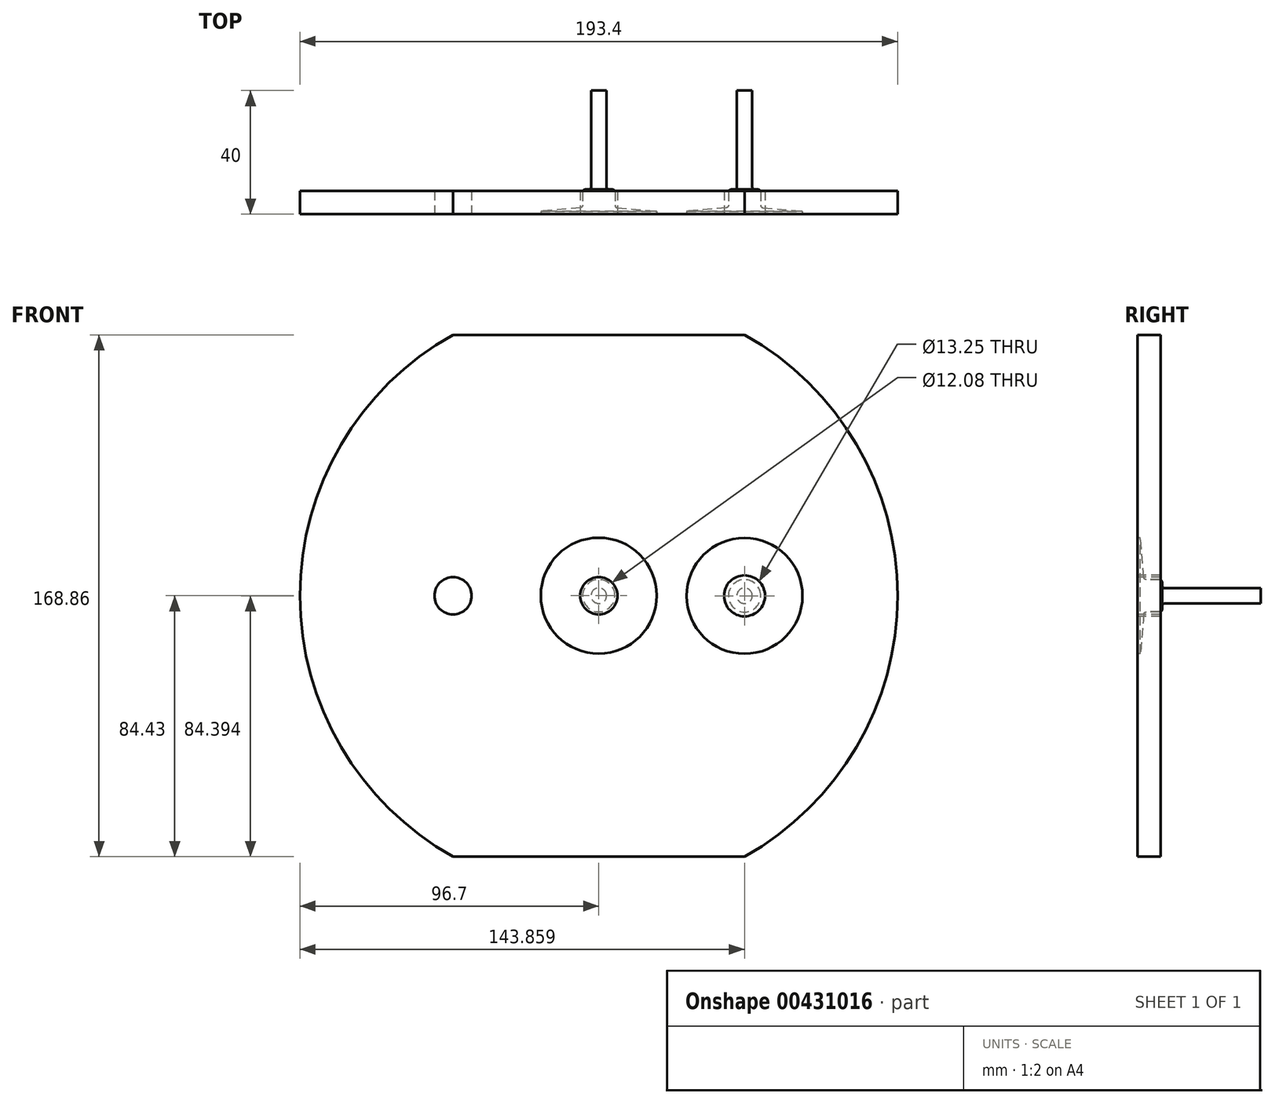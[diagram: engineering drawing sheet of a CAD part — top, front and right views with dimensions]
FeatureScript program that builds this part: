
annotation { "Feature Type Name" : "Feature", "Feature Type Description" : "" }
export const myFeature = defineFeature(function(context is Context, id is Id, definition is map)
    precondition{}
    {
        {
            var Q0;
            Q0=qCreatedBy(makeId("Front.planeOp"),FACE);
            var sketch = newSketch(context, id + "F0", { "sketchPlane" : qUnion([Q0])});
            skCircle(sketch, "E0", {"center": v(0, 0) * mm, "radius": 5.22 * mm});
            skPoint(sketch, "E0.first.point", {"position": v(-0.14, 5.22) * mm});
            skPoint(sketch, "E0.second.point", {"position": v(0.18, -5.22) * mm});
            skPoint(sketch, "E0.third.point", {"position": v(5.22, 0.15) * mm});
            skSolve(sketch);
        }
        {
            var Q0;
            Q0=qCreatedBy(makeId("Front.planeOp"),FACE);
            var sketch = newSketch(context, id + "F1", { "sketchPlane" : qUnion([Q0])});
            skCircle(sketch, "E1.0", {"center": v(0, 0) * mm, "radius": 5.22 * mm});
            skLineSegment(sketch, "E2", {"start": v(0, 125) * mm, "end": v(0, -125) * mm, "construction": true});
            skLineSegment(sketch, "E3", {"start": v(-125, 0) * mm, "end": v(125, 0) * mm, "construction": true});
            skArc(sketch, "E4", {"start": v(-3.61, 24.74) * mm, "mid": v(1.57, -24.95) * mm, "end": v(0.48, 25) * mm, "construction": true});
            skCircle(sketch, "E5", {"center": v(0, 0) * mm, "radius": 23.24 * mm, "construction": true});
            skCircle(sketch, "E6", {"center": v(0, 0) * mm, "radius": 21.43 * mm, "construction": true});
            skLineSegment(sketch, "E7", {"start": v(0, 0) * mm, "end": v(-4.4, 25.96) * mm, "construction": true});
            skLineSegment(sketch, "E8", {"start": v(0, 0) * mm, "end": v(1.13, 26.88) * mm, "construction": true});
            skFitSpline(sketch, "E9", {"points": [v(-3.61, 24.74) * mm, v(-2.7, 23.08) * mm, v(-2.2, 21.32) * mm, v(-1.5, 20.62) * mm], "startDerivative": vector(3.33, -4.08) * mm, "endDerivative": vector(3.08, -2.02) * mm});
            skFitSpline(sketch, "E10.MirrorCS", {"points": [v(0.48, 25) * mm, v(-0.2, 23.23) * mm, v(-0.5, 21.43) * mm, v(-1.1, 20.65) * mm], "startDerivative": vector(-2.8, -4.47) * mm, "endDerivative": vector(-2.8, -2.4) * mm});
            skArc(sketch, "E11", {"start": v(-2.2, 21.32) * mm, "mid": v(-1.35, 21.39) * mm, "end": v(-0.5, 21.43) * mm});
            skArc(sketch, "E12", {"start": v(-4.17, 24.65) * mm, "mid": v(-3.9, 24.7) * mm, "end": v(-3.61, 24.74) * mm});
            skArc(sketch, "E13.trimOffspring", {"start": v(0.48, 25) * mm, "mid": v(0.77, 24.99) * mm, "end": v(1.05, 24.98) * mm});
            skArc(sketch, "E14.1.0", {"start": v(-4.72, 24.55) * mm, "mid": v(-4.45, 24.6) * mm, "end": v(-4.17, 24.65) * mm});
            skArc(sketch, "E14.1.1", {"start": v(-9.2, 23.24) * mm, "mid": v(-8.94, 23.35) * mm, "end": v(-8.68, 23.45) * mm});
            skArc(sketch, "E14.1.2", {"start": v(-6.58, 20.4) * mm, "mid": v(-5.76, 20.64) * mm, "end": v(-4.94, 20.86) * mm});
            skArc(sketch, "E14.2.0", {"start": v(-9.72, 23.03) * mm, "mid": v(-9.46, 23.14) * mm, "end": v(-9.2, 23.24) * mm});
            skArc(sketch, "E14.2.1", {"start": v(-13.84, 20.82) * mm, "mid": v(-13.6, 20.98) * mm, "end": v(-13.36, 21.13) * mm});
            skArc(sketch, "E14.2.2", {"start": v(-10.68, 18.58) * mm, "mid": v(-9.93, 19) * mm, "end": v(-9.16, 19.37) * mm});
            skArc(sketch, "E14.3.0", {"start": v(-14.3, 20.5) * mm, "mid": v(-14.07, 20.67) * mm, "end": v(-13.84, 20.82) * mm});
            skArc(sketch, "E14.3.1", {"start": v(-17.86, 17.5) * mm, "mid": v(-17.66, 17.7) * mm, "end": v(-17.46, 17.89) * mm});
            skArc(sketch, "E14.3.2", {"start": v(-14.3, 15.96) * mm, "mid": v(-13.66, 16.51) * mm, "end": v(-13, 17.04) * mm});
            skArc(sketch, "E14.4.0", {"start": v(-18.25, 17.08) * mm, "mid": v(-18.06, 17.29) * mm, "end": v(-17.86, 17.5) * mm});
            skArc(sketch, "E14.4.1", {"start": v(-21.1, 13.4) * mm, "mid": v(-20.96, 13.63) * mm, "end": v(-20.8, 13.87) * mm});
            skArc(sketch, "E14.4.2", {"start": v(-17.31, 12.63) * mm, "mid": v(-16.8, 13.31) * mm, "end": v(-16.25, 13.97) * mm});
            skArc(sketch, "E14.5.0", {"start": v(-21.4, 12.92) * mm, "mid": v(-21.26, 13.16) * mm, "end": v(-21.1, 13.4) * mm});
            skArc(sketch, "E14.5.1", {"start": v(-23.43, 8.71) * mm, "mid": v(-23.33, 8.98) * mm, "end": v(-23.23, 9.24) * mm});
            skArc(sketch, "E14.5.2", {"start": v(-19.56, 8.76) * mm, "mid": v(-19.2, 9.53) * mm, "end": v(-18.8, 10.29) * mm});
            skArc(sketch, "E14.6.0", {"start": v(-23.62, 8.18) * mm, "mid": v(-23.53, 8.45) * mm, "end": v(-23.43, 8.71) * mm});
            skArc(sketch, "E14.6.1", {"start": v(-24.73, 3.65) * mm, "mid": v(-24.69, 3.93) * mm, "end": v(-24.64, 4.2) * mm});
            skArc(sketch, "E14.6.2", {"start": v(-20.95, 4.5) * mm, "mid": v(-20.76, 5.33) * mm, "end": v(-20.53, 6.15) * mm});
            skArc(sketch, "E14.7.0", {"start": v(-24.8, 3.1) * mm, "mid": v(-24.77, 3.37) * mm, "end": v(-24.73, 3.65) * mm});
            skArc(sketch, "E14.7.1", {"start": v(-24.95, -1.57) * mm, "mid": v(-24.97, -1.29) * mm, "end": v(-24.98, -1) * mm});
            skArc(sketch, "E14.7.2", {"start": v(-21.43, 0.04) * mm, "mid": v(-21.41, 0.9) * mm, "end": v(-21.36, 1.75) * mm});
            skArc(sketch, "E14.8.0", {"start": v(-24.9, -2.13) * mm, "mid": v(-24.93, -1.85) * mm, "end": v(-24.95, -1.57) * mm});
            skArc(sketch, "E14.8.1", {"start": v(-24.08, -6.72) * mm, "mid": v(-24.15, -6.45) * mm, "end": v(-24.22, -6.18) * mm});
            skArc(sketch, "E14.8.2", {"start": v(-20.97, -4.41) * mm, "mid": v(-21.13, -3.57) * mm, "end": v(-21.26, -2.73) * mm});
            skArc(sketch, "E14.9.0", {"start": v(-23.92, -7.26) * mm, "mid": v(-24, -7) * mm, "end": v(-24.08, -6.72) * mm});
            skArc(sketch, "E14.9.1", {"start": v(-22.15, -11.58) * mm, "mid": v(-22.28, -11.33) * mm, "end": v(-22.4, -11.08) * mm});
            skArc(sketch, "E14.9.2", {"start": v(-19.6, -8.68) * mm, "mid": v(-19.93, -7.9) * mm, "end": v(-20.23, -7.09) * mm});
            skArc(sketch, "E14.10.0", {"start": v(-21.89, -12.08) * mm, "mid": v(-22.02, -11.83) * mm, "end": v(-22.15, -11.58) * mm});
            skArc(sketch, "E14.10.1", {"start": v(-19.26, -15.94) * mm, "mid": v(-19.44, -15.72) * mm, "end": v(-19.62, -15.5) * mm});
            skArc(sketch, "E14.10.2", {"start": v(-17.36, -12.56) * mm, "mid": v(-17.85, -11.86) * mm, "end": v(-18.3, -11.14) * mm});
            skArc(sketch, "E14.11.0", {"start": v(-18.9, -16.37) * mm, "mid": v(-19.08, -16.15) * mm, "end": v(-19.26, -15.94) * mm});
            skArc(sketch, "E14.11.1", {"start": v(-15.53, -19.6) * mm, "mid": v(-15.75, -19.42) * mm, "end": v(-15.97, -19.24) * mm});
            skArc(sketch, "E14.11.2", {"start": v(-14.37, -15.9) * mm, "mid": v(-15, -15.31) * mm, "end": v(-15.6, -14.7) * mm});
            skArc(sketch, "E14.12.0", {"start": v(-15.08, -19.94) * mm, "mid": v(-15.3, -19.77) * mm, "end": v(-15.53, -19.6) * mm});
            skArc(sketch, "E14.12.1", {"start": v(-11.12, -22.4) * mm, "mid": v(-11.37, -22.27) * mm, "end": v(-11.62, -22.14) * mm});
            skArc(sketch, "E14.12.2", {"start": v(-10.75, -18.54) * mm, "mid": v(-11.48, -18.1) * mm, "end": v(-12.2, -17.62) * mm});
            skArc(sketch, "E14.13.0", {"start": v(-10.6, -22.64) * mm, "mid": v(-10.86, -22.52) * mm, "end": v(-11.12, -22.4) * mm});
            skArc(sketch, "E14.13.1", {"start": v(-6.22, -24.21) * mm, "mid": v(-6.49, -24.14) * mm, "end": v(-6.76, -24.07) * mm});
            skArc(sketch, "E14.13.2", {"start": v(-6.66, -20.37) * mm, "mid": v(-7.47, -20.09) * mm, "end": v(-8.26, -19.77) * mm});
            skArc(sketch, "E14.14.0", {"start": v(-5.67, -24.35) * mm, "mid": v(-5.94, -24.28) * mm, "end": v(-6.22, -24.21) * mm});
            skArc(sketch, "E14.14.1", {"start": v(-1.05, -24.98) * mm, "mid": v(-1.33, -24.96) * mm, "end": v(-1.6, -24.95) * mm});
            skArc(sketch, "E14.14.2", {"start": v(-2.28, -21.3) * mm, "mid": v(-3.13, -21.2) * mm, "end": v(-3.97, -21.06) * mm});
            skArc(sketch, "E14.15.0", {"start": v(-0.48, -25) * mm, "mid": v(-0.77, -24.99) * mm, "end": v(-1.05, -24.98) * mm});
            skArc(sketch, "E14.15.1", {"start": v(4.17, -24.65) * mm, "mid": v(3.9, -24.7) * mm, "end": v(3.61, -24.74) * mm});
            skArc(sketch, "E14.15.2", {"start": v(2.2, -21.32) * mm, "mid": v(1.35, -21.39) * mm, "end": v(0.5, -21.43) * mm});
            skArc(sketch, "E14.16.0", {"start": v(4.72, -24.55) * mm, "mid": v(4.45, -24.6) * mm, "end": v(4.17, -24.65) * mm});
            skArc(sketch, "E14.16.1", {"start": v(9.2, -23.24) * mm, "mid": v(8.94, -23.35) * mm, "end": v(8.68, -23.45) * mm});
            skArc(sketch, "E14.16.2", {"start": v(6.58, -20.4) * mm, "mid": v(5.76, -20.64) * mm, "end": v(4.94, -20.86) * mm});
            skArc(sketch, "E14.17.0", {"start": v(9.72, -23.03) * mm, "mid": v(9.46, -23.14) * mm, "end": v(9.2, -23.24) * mm});
            skArc(sketch, "E14.17.1", {"start": v(13.84, -20.82) * mm, "mid": v(13.6, -20.98) * mm, "end": v(13.36, -21.13) * mm});
            skArc(sketch, "E14.17.2", {"start": v(10.68, -18.58) * mm, "mid": v(9.93, -19) * mm, "end": v(9.16, -19.37) * mm});
            skArc(sketch, "E14.18.0", {"start": v(14.3, -20.5) * mm, "mid": v(14.07, -20.67) * mm, "end": v(13.84, -20.82) * mm});
            skArc(sketch, "E14.18.1", {"start": v(17.86, -17.5) * mm, "mid": v(17.66, -17.7) * mm, "end": v(17.46, -17.89) * mm});
            skArc(sketch, "E14.18.2", {"start": v(14.3, -15.96) * mm, "mid": v(13.66, -16.51) * mm, "end": v(13, -17.04) * mm});
            skArc(sketch, "E14.19.0", {"start": v(18.25, -17.08) * mm, "mid": v(18.06, -17.29) * mm, "end": v(17.86, -17.5) * mm});
            skArc(sketch, "E14.19.1", {"start": v(21.1, -13.4) * mm, "mid": v(20.96, -13.63) * mm, "end": v(20.8, -13.87) * mm});
            skArc(sketch, "E14.19.2", {"start": v(17.31, -12.63) * mm, "mid": v(16.8, -13.31) * mm, "end": v(16.25, -13.97) * mm});
            skArc(sketch, "E14.20.0", {"start": v(21.4, -12.92) * mm, "mid": v(21.26, -13.16) * mm, "end": v(21.1, -13.4) * mm});
            skArc(sketch, "E14.20.1", {"start": v(23.43, -8.71) * mm, "mid": v(23.33, -8.98) * mm, "end": v(23.23, -9.24) * mm});
            skArc(sketch, "E14.20.2", {"start": v(19.56, -8.76) * mm, "mid": v(19.2, -9.53) * mm, "end": v(18.8, -10.29) * mm});
            skArc(sketch, "E14.21.0", {"start": v(23.62, -8.18) * mm, "mid": v(23.53, -8.45) * mm, "end": v(23.43, -8.71) * mm});
            skArc(sketch, "E14.21.1", {"start": v(24.73, -3.65) * mm, "mid": v(24.69, -3.93) * mm, "end": v(24.64, -4.2) * mm});
            skArc(sketch, "E14.21.2", {"start": v(20.95, -4.5) * mm, "mid": v(20.76, -5.33) * mm, "end": v(20.53, -6.15) * mm});
            skArc(sketch, "E14.22.0", {"start": v(24.8, -3.1) * mm, "mid": v(24.77, -3.37) * mm, "end": v(24.73, -3.65) * mm});
            skArc(sketch, "E14.22.1", {"start": v(24.95, 1.57) * mm, "mid": v(24.97, 1.29) * mm, "end": v(24.98, 1) * mm});
            skArc(sketch, "E14.22.2", {"start": v(21.43, -0.04) * mm, "mid": v(21.41, -0.9) * mm, "end": v(21.36, -1.75) * mm});
            skArc(sketch, "E14.23.0", {"start": v(24.9, 2.13) * mm, "mid": v(24.93, 1.85) * mm, "end": v(24.95, 1.57) * mm});
            skArc(sketch, "E14.23.1", {"start": v(24.08, 6.72) * mm, "mid": v(24.15, 6.45) * mm, "end": v(24.22, 6.18) * mm});
            skArc(sketch, "E14.23.2", {"start": v(20.97, 4.41) * mm, "mid": v(21.13, 3.57) * mm, "end": v(21.26, 2.73) * mm});
            skArc(sketch, "E14.24.0", {"start": v(23.92, 7.26) * mm, "mid": v(24, 7) * mm, "end": v(24.08, 6.72) * mm});
            skArc(sketch, "E14.24.1", {"start": v(22.15, 11.58) * mm, "mid": v(22.28, 11.33) * mm, "end": v(22.4, 11.08) * mm});
            skArc(sketch, "E14.24.2", {"start": v(19.6, 8.68) * mm, "mid": v(19.93, 7.9) * mm, "end": v(20.23, 7.09) * mm});
            skArc(sketch, "E14.25.0", {"start": v(21.89, 12.08) * mm, "mid": v(22.02, 11.83) * mm, "end": v(22.15, 11.58) * mm});
            skArc(sketch, "E14.25.1", {"start": v(19.26, 15.94) * mm, "mid": v(19.44, 15.72) * mm, "end": v(19.62, 15.5) * mm});
            skArc(sketch, "E14.25.2", {"start": v(17.36, 12.56) * mm, "mid": v(17.85, 11.86) * mm, "end": v(18.3, 11.14) * mm});
            skArc(sketch, "E14.26.0", {"start": v(18.9, 16.37) * mm, "mid": v(19.08, 16.15) * mm, "end": v(19.26, 15.94) * mm});
            skArc(sketch, "E14.26.1", {"start": v(15.53, 19.6) * mm, "mid": v(15.75, 19.42) * mm, "end": v(15.97, 19.24) * mm});
            skArc(sketch, "E14.26.2", {"start": v(14.37, 15.9) * mm, "mid": v(15, 15.31) * mm, "end": v(15.6, 14.7) * mm});
            skArc(sketch, "E14.27.0", {"start": v(15.08, 19.94) * mm, "mid": v(15.3, 19.77) * mm, "end": v(15.53, 19.6) * mm});
            skArc(sketch, "E14.27.1", {"start": v(11.12, 22.4) * mm, "mid": v(11.37, 22.27) * mm, "end": v(11.62, 22.14) * mm});
            skArc(sketch, "E14.27.2", {"start": v(10.75, 18.54) * mm, "mid": v(11.48, 18.1) * mm, "end": v(12.2, 17.62) * mm});
            skArc(sketch, "E14.28.0", {"start": v(10.6, 22.64) * mm, "mid": v(10.86, 22.52) * mm, "end": v(11.12, 22.4) * mm});
            skArc(sketch, "E14.28.1", {"start": v(6.22, 24.21) * mm, "mid": v(6.49, 24.14) * mm, "end": v(6.76, 24.07) * mm});
            skArc(sketch, "E14.28.2", {"start": v(6.66, 20.37) * mm, "mid": v(7.47, 20.09) * mm, "end": v(8.26, 19.77) * mm});
            skArc(sketch, "E14.29.0", {"start": v(5.67, 24.35) * mm, "mid": v(5.94, 24.28) * mm, "end": v(6.22, 24.21) * mm});
            skArc(sketch, "E14.29.1", {"start": v(1.05, 24.98) * mm, "mid": v(1.33, 24.96) * mm, "end": v(1.6, 24.95) * mm});
            skArc(sketch, "E14.29.2", {"start": v(2.28, 21.3) * mm, "mid": v(3.13, 21.2) * mm, "end": v(3.97, 21.06) * mm});
            skArc(sketch, "E15", {"start": v(-3.61, 24.74) * mm, "mid": v(-1.57, 24.95) * mm, "end": v(0.48, 25) * mm});
            skCircle(sketch, "E16", {"center": v(-47.16, -0.04) * mm, "radius": 21.4 * mm, "construction": true});
            skPoint(sketch, "E16.first.point", {"position": v(-56.55, 19.18) * mm});
            skPoint(sketch, "E16.second.point", {"position": v(-28.26, -10.06) * mm});
            skPoint(sketch, "E16.third.point", {"position": v(-59.13, -17.76) * mm});
            skLineSegment(sketch, "E17", {"start": v(-47.16, 125) * mm, "end": v(-47.16, -171.02) * mm, "construction": true});
            skLineSegment(sketch, "E18.MirrorCS", {"start": v(47.16, 125) * mm, "end": v(47.16, -171.02) * mm, "construction": true});
            skCircle(sketch, "E19.MirrorC", {"center": v(47.16, -0.04) * mm, "radius": 21.4 * mm, "construction": true});
            skSolve(sketch);
        }
        {
            var Q0;
            Q0=qCreatedBy(makeId("Right.planeOp"),FACE);
            var sketch = newSketch(context, id + "F2", { "sketchPlane" : qUnion([Q0])});
            skLineSegment(sketch, "E20.bottom", {"start": v(5, 0) * mm, "end": v(0, 0) * mm});
            skPoint(sketch, "E21.0", {"position": v(0, 5.22) * mm});
            skLineSegment(sketch, "E22.bottom", {"start": v(0, 0) * mm, "end": v(40, 0) * mm});
            skLineSegment(sketch, "E22.top", {"start": v(2.92, 5.22) * mm, "end": v(7.2, 5.22) * mm});
            skLineSegment(sketch, "E22.right", {"start": v(40, 0) * mm, "end": v(40, 2.5) * mm});
            skLineSegment(sketch, "E23.top", {"start": v(40, 2.5) * mm, "end": v(8.8, 2.5) * mm});
            skLineSegment(sketch, "E23.right", {"start": v(8, 4.42) * mm, "end": v(8, 3.3) * mm});
            skPoint(sketch, "E24.orphan", {"position": v(40, 5.22) * mm});
            skPoint(sketch, "E25.visualSharp", {"position": v(8, 5.22) * mm});
            skArc(sketch, "E25.filletArc", {"start": v(8, 4.42) * mm, "mid": v(7.77, 4.99) * mm, "end": v(7.2, 5.22) * mm});
            skPoint(sketch, "E26.visualSharp", {"position": v(8, 2.5) * mm});
            skArc(sketch, "E26.filletArc", {"start": v(8, 3.3) * mm, "mid": v(8.23, 2.73) * mm, "end": v(8.8, 2.5) * mm});
            skLineSegment(sketch, "E27.0", {"start": v(0, -25) * mm, "end": v(0, 0) * mm, "construction": true});
            skLineSegment(sketch, "E28", {"start": v(0, 0) * mm, "end": v(0, 5.22) * mm});
            skLineSegment(sketch, "E29.top", {"start": v(0, 18.75) * mm, "end": v(1, 18.75) * mm});
            skLineSegment(sketch, "E29.left", {"start": v(0, 5.22) * mm, "end": v(0, 18.75) * mm});
            skArc(sketch, "E30.filletArc", {"start": v(2.12, 5.95) * mm, "mid": v(2.38, 5.43) * mm, "end": v(2.92, 5.22) * mm});
            skLineSegment(sketch, "E31", {"start": v(1, 18.75) * mm, "end": v(2.12, 5.95) * mm});
            skSolve(sketch);
        }
        {
            var Q0;
            Q0=makeQuery(id+"F2.imprint","IMPRINT",FACE,{"disambiguationData":[TD([[makeQuery(id+"F2.imprint","IMPRINT",EDGE,{"derivedFrom":sQuery(id+"F2.wireOp",EDGE,"E20.top")}),1.0]])]});
            var Q1;
            {var subQ5=sQuery(id+"F2.wireOp",EDGE,"E22.left");Q1=makeQuery(id+"F2.imprint","IMPRINT",FACE,{"disambiguationData":[TD([[makeQuery(id+"F2.imprint","IMPRINT",EDGE,{"derivedFrom":subQ5}),-1.0]])]});}
            var Q2;
            {var subQ0=sQuery(id+"F2.wireOp",EDGE,"E22.right");Q2=makeQuery(id+"F2.imprint","IMPRINT",FACE,{"disambiguationData":[TD([[makeQuery(id+"F2.imprint","IMPRINT",EDGE,{"derivedFrom":subQ0}),1.0]])]});}
            var Q3;
            Q3=sQuery(id+"F2.wireOp",EDGE,"E22.bottom");
            revolve(context, id + "F3", {"entities" : qUnion([Q0, Q1, Q2]), "axis" : qUnion([Q3]), "revolveType" : RevolveType.FULL});
        }
        {
            var Q0;
            Q0=sQuery(id+"F1.wireOp",EDGE,"E3");
            cPoint(context, id + "F4", {"entities" : qUnion([Q0]), "parameter" : 0.5});
        }
        {
            var Q0;
            Q0=makeQuery(id+"F3.opRevolve","SWEPT_BODY",BODY,{"disambiguationData":[OSD([sQuery(id+"F2.wireOp",EDGE,"E20.top"),sQuery(id+"F2.wireOp",EDGE,"E20.left"),sQuery(id+"F2.wireOp",EDGE,"E20.right"),sQuery(id+"F2.wireOp",EDGE,"E22.top"),sQuery(id+"F2.wireOp",EDGE,"b44fa62e-ace7-4b5d-8e5e-86d7856472b4"),sQuery(id+"F2.wireOp",EDGE,"foJHeyPD-UMAC-skvq-aQiw-TZUx3iRgKaAy.bottom"),sQuery(id+"F2.wireOp",EDGE,"foJHeyPD-UMAC-skvq-aQiw-TZUx3iRgKaAy.top"),sQuery(id+"F2.wireOp",EDGE,"foJHeyPD-UMAC-skvq-aQiw-TZUx3iRgKaAy.right"),sQuery(id+"F2.wireOp",EDGE,"a05660c1-c4d1-4545-8ea9-213eea5170590.MirrorCS"),sQuery(id+"F2.wireOp",EDGE,"ed72f9f3-1d14-4217-9ee5-c56edde265eb0.MirrorCS"),sQuery(id+"F2.wireOp",EDGE,"6f369c07-5317-4975-a260-c799c4c0cf5f0.MirrorCS"),sQuery(id+"F2.wireOp",EDGE,"141536f0-b08a-42de-a3e6-616160e136e60.MirrorCS"),sQuery(id+"F2.wireOp",EDGE,"fcf2f710-ba7c-4687-9936-d15eea83fc5b.filletArc"),sQuery(id+"F2.wireOp",EDGE,"117e4287-3e94-4b07-8f2a-80edc98b9095.filletArc"),sQuery(id+"F2.wireOp",EDGE,"5666ae85-9655-4590-806c-70a619aee00b.filletArc"),sQuery(id+"F2.wireOp",EDGE,"109780fe-2bf1-43e8-bdb1-ecf59667137d.filletArc"),sQuery(id+"F2.wireOp",EDGE,"ogJhYKfy-YAjB-aqbb-kaJ7-WClFPnS7C8W1.bottom")])]});
            var Q1;
            Q1 = qCreatedBy(id + "F4" ,VERTEX);
            var Q2;
            Q2=sQuery(id+"F1.wireOp",VERTEX,"E16.center");
            transform(context, id + "F5", {"entities" : qUnion([Q0]), "transformType" : TransformType.TRANSLATION_ENTITY, "oppositeDirectionEntity" : false, "transformLine" : qUnion([Q1, Q2]), "makeCopy" : true});
        }
        {
            var Q0;
            Q0=makeQuery(id+"F3.opRevolve","SWEPT_BODY",BODY,{"disambiguationData":[OSD([sQuery(id+"F2.wireOp",EDGE,"E22.bottom"),sQuery(id+"F2.wireOp",EDGE,"E22.top"),sQuery(id+"F2.wireOp",EDGE,"E22.right"),sQuery(id+"F2.wireOp",EDGE,"E23.top"),sQuery(id+"F2.wireOp",EDGE,"E23.right"),sQuery(id+"F2.wireOp",EDGE,"E25.filletArc"),sQuery(id+"F2.wireOp",EDGE,"E26.filletArc"),sQuery(id+"F2.wireOp",EDGE,"E28"),sQuery(id+"F2.wireOp",EDGE,"E29.top"),sQuery(id+"F2.wireOp",EDGE,"E29.left"),sQuery(id+"F2.wireOp",EDGE,"E29.right"),sQuery(id+"F2.wireOp",EDGE,"E30.filletArc"),sQuery(id+"F2.wireOp",EDGE,"e0f4d18f-0478-4621-8dee-925c7302a5a3.filletArc")])]});
            var Q1;
            Q1=sQuery(id+"F1.wireOp",VERTEX,"E1.0.center");
            var Q2;
            Q2=sQuery(id+"F1.wireOp",VERTEX,"E19.MirrorC.center");
            transform(context, id + "F6", {"entities" : qUnion([Q0]), "transformType" : TransformType.TRANSLATION_ENTITY, "oppositeDirectionEntity" : false, "transformLine" : qUnion([Q1, Q2]), "makeCopy" : true});
        }
        {
            var Q0;
            Q0=qCreatedBy(makeId("Front.planeOp"),FACE);
            var sketch = newSketch(context, id + "F7", { "sketchPlane" : qUnion([Q0])});
            skLineSegment(sketch, "E32.bottom", {"start": v(-47.16, 84.43) * mm, "end": v(47.16, 84.43) * mm});
            skLineSegment(sketch, "E33.0", {"start": v(-125, 0) * mm, "end": v(125, 0) * mm});
            skArc(sketch, "E34", {"start": v(-47.16, 84.43) * mm, "mid": v(-96.7, 0) * mm, "end": v(-47.16, -84.43) * mm});
            skLineSegment(sketch, "E35.MirrorCS", {"start": v(-47.16, -84.43) * mm, "end": v(47.16, -84.43) * mm});
            skArc(sketch, "E36.trimOffspring", {"start": v(47.16, -84.43) * mm, "mid": v(96.7, 0) * mm, "end": v(47.16, 84.43) * mm});
            skCircle(sketch, "E37.0", {"center": v(-47.16, -0.04) * mm, "radius": 6.02 * mm});
            skCircle(sketch, "E38.0", {"center": v(0, 0) * mm, "radius": 6.02 * mm});
            skCircle(sketch, "E39.0", {"center": v(47.16, -0.04) * mm, "radius": 6.02 * mm});
            skCircle(sketch, "E40", {"center": v(47.16, -0.04) * mm, "radius": 6.62 * mm});
            skCircle(sketch, "E41", {"center": v(0, 0) * mm, "radius": 6.04 * mm});
            skSolve(sketch);
        }
        {
            var Q0;
            {var subQ9=sQuery(id+"F7.wireOp",EDGE,"E35.MirrorCS");Q0=makeQuery(id+"F7.imprint","IMPRINT",FACE,{"disambiguationData":[TD([[makeQuery(id+"F7.imprint","IMPRINT",EDGE,{"derivedFrom":subQ9}),1.0]])]});}
            var Q1;
            {var subQ11=sQuery(id+"F7.wireOp",EDGE,"E32.bottom");Q1=makeQuery(id+"F7.imprint","IMPRINT",FACE,{"disambiguationData":[TD([[makeQuery(id+"F7.imprint","IMPRINT",EDGE,{"derivedFrom":subQ11}),-1.0]])]});}
            var Q2;
            Q2=sQuery(id+"F7.wireOp",EDGE,"E37.0");
            extrude(context, id + "F8", {"entities" : qUnion([Q0, Q1]), "surfaceEntities" : qUnion([Q2]), "oppositeDirection" : true, "depth" : 7.5 * mm});
        }
        {
            var Q0;
            Q0=makeQuery(id+"F5.opPattern","COPY",BODY,{"derivedFrom":makeQuery(id+"F3.opRevolve","SWEPT_BODY",BODY,{"disambiguationData":[OSD([sQuery(id+"F2.wireOp",EDGE,"E22.bottom"),sQuery(id+"F2.wireOp",EDGE,"E22.top"),sQuery(id+"F2.wireOp",EDGE,"E22.right"),sQuery(id+"F2.wireOp",EDGE,"E23.top"),sQuery(id+"F2.wireOp",EDGE,"E23.right"),sQuery(id+"F2.wireOp",EDGE,"E25.filletArc"),sQuery(id+"F2.wireOp",EDGE,"E26.filletArc"),sQuery(id+"F2.wireOp",EDGE,"E28")])]}),"instanceName":"1"});
            deleteBodies(context, id + "F9", {"entities" : qUnion([Q0])});
        }
    });
